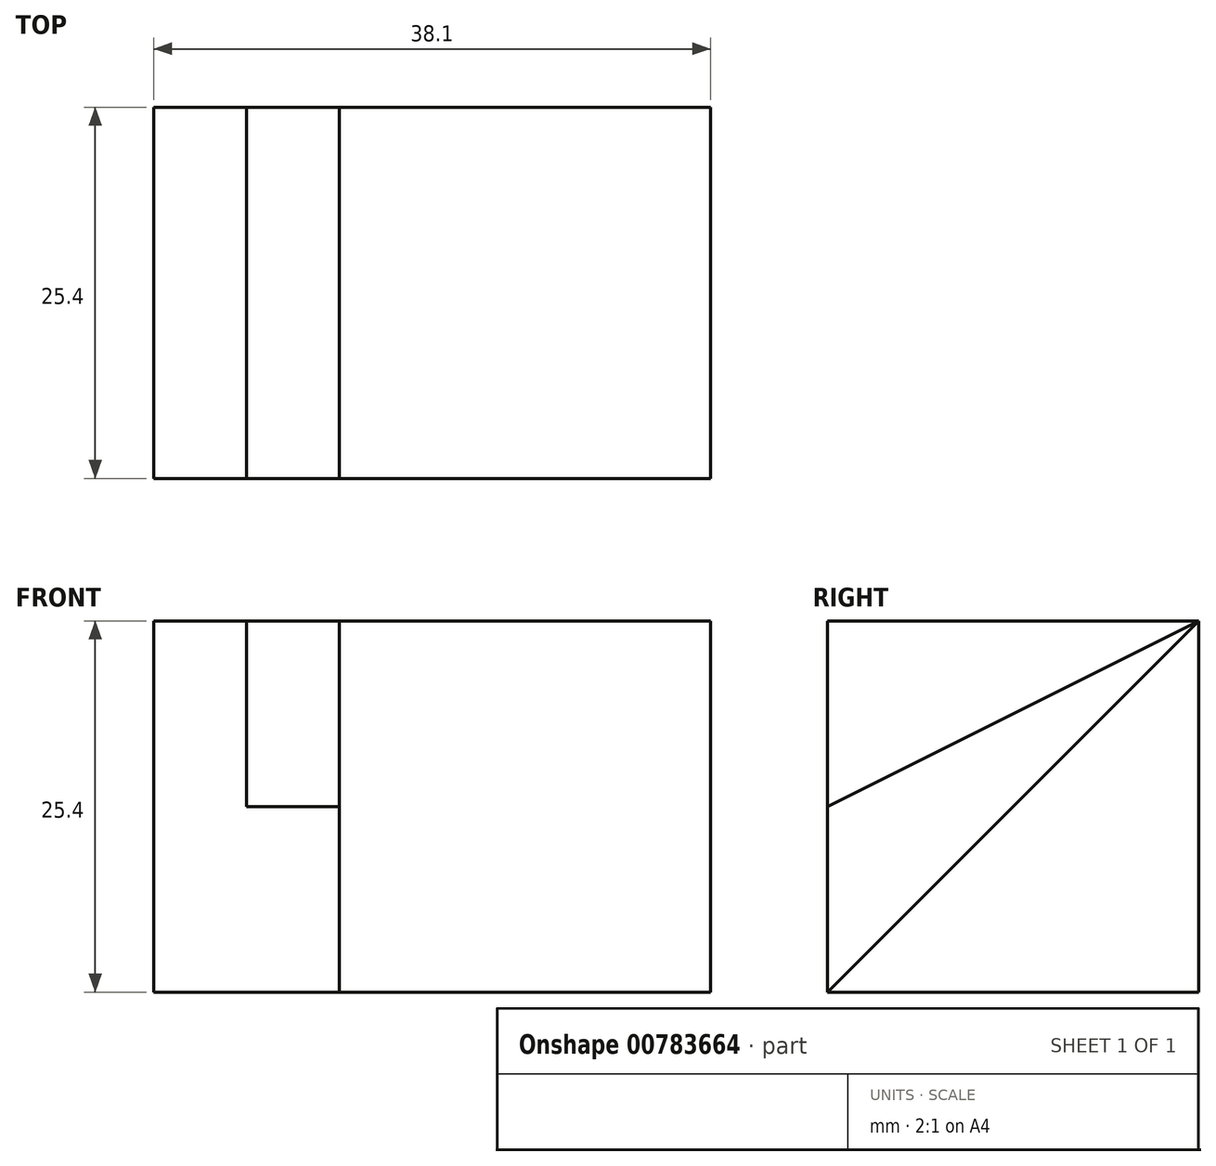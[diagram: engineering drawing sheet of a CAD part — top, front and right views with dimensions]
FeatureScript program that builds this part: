
annotation { "Feature Type Name" : "Feature", "Feature Type Description" : "" }
export const myFeature = defineFeature(function(context is Context, id is Id, definition is map)
    precondition{}
    {
        {
            var Q0;
            Q0=qCreatedBy(makeId("Front.planeOp"),FACE);
            var sketch = newSketch(context, id + "F0", { "sketchPlane" : qUnion([Q0])});
            skLineSegment(sketch, "E0", {"start": v(0, 0) * mm, "end": v(38.1, 0) * mm});
            skLineSegment(sketch, "E1", {"start": v(38.1, 0) * mm, "end": v(38.1, 25.4) * mm});
            skLineSegment(sketch, "E2", {"start": v(38.1, 25.4) * mm, "end": v(0, 25.4) * mm});
            skLineSegment(sketch, "E3", {"start": v(0, 25.4) * mm, "end": v(0, 0) * mm});
            skSolve(sketch);
        }
        {
            var Q0;
            Q0 = qSketchRegion(id + "F0", true);
            extrude(context, id + "F1", {"entities" : qUnion([Q0]), "depth" : 25.4 * mm, "offsetDistance" : 25.4 * mm});
        }
        {
            var Q0;
            Q0=makeQuery(id+"F1.opExtrude","SWEPT_FACE",FACE,{"disambiguationData":[OSD([sQuery(id+"F0.wireOp",EDGE,"E1")])]});
            var sketch = newSketch(context, id + "F2", { "sketchPlane" : qUnion([Q0])});
            skLineSegment(sketch, "E4", {"start": v(0, 25.4) * mm, "end": v(-25.4, 0) * mm});
            skSolve(sketch);
        }
        {
            var Q0;
            Q0=makeQuery(id+"F2.imprint","IMPRINT",FACE,{"disambiguationData":[TD([[makeQuery(id+"F2.imprint","IMPRINT",EDGE,{"derivedFrom":sQuery(id+"F2.wireOp",EDGE,"E4")}),-1.0]])]});
            extrude(context, id + "F3", {"entities" : qUnion([Q0]), "operationType" : NewBodyOperationType.REMOVE, "oppositeDirection" : true, "depth" : 25.4 * mm, "offsetDistance" : 25.4 * mm});
        }
        {
            var Q0;
            Q0=makeQuery(id+"F3.boolean.opBoolean","COPY",FACE,{"derivedFrom":makeQuery(id+"F3.opExtrude","CAP_FACE",FACE,{"disambiguationData":[OSD([sQuery(id+"F0.wireOp",EDGE,"E1"),sQuery(id+"F0.wireOp",EDGE,"E2"),sQuery(id+"F2.wireOp",EDGE,"E4")])],"isStart":false})});
            var sketch = newSketch(context, id + "F4", { "sketchPlane" : qUnion([Q0])});
            skLineSegment(sketch, "E5", {"start": v(0, 25.4) * mm, "end": v(-25.4, 12.7) * mm});
            skSolve(sketch);
        }
        {
            var Q0;
            {var subQ0=sQuery(id+"F4.wireOp",EDGE,"E5");Q0=makeQuery(id+"F4.imprint","IMPRINT",FACE,{"disambiguationData":[TD([[makeQuery(id+"F4.imprint","IMPRINT",EDGE,{"derivedFrom":subQ0}),-1.0]])]});}
            extrude(context, id + "F5", {"entities" : qUnion([Q0]), "operationType" : NewBodyOperationType.REMOVE, "oppositeDirection" : true, "depth" : 6.35 * mm, "offsetDistance" : 25.4 * mm});
        }
    });
